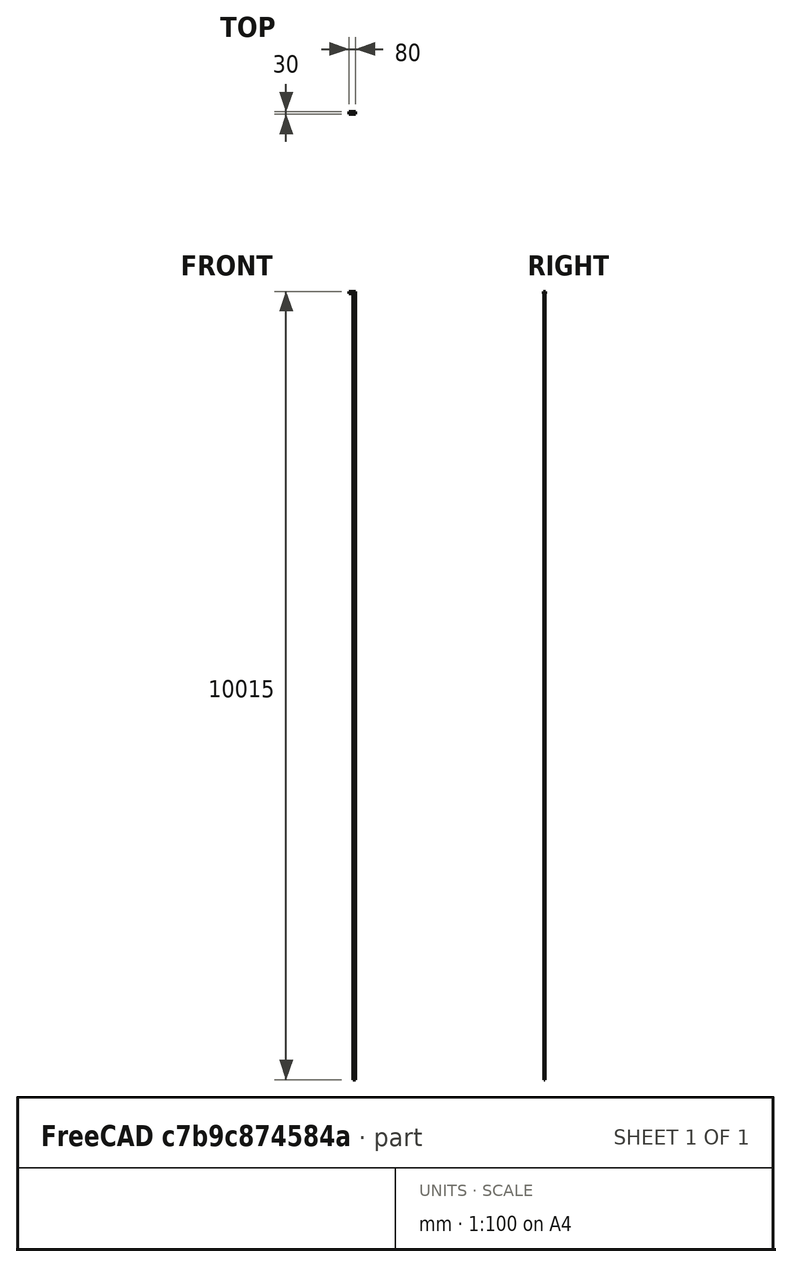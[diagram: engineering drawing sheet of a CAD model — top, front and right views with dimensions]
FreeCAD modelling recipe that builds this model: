
FCSTD DOCUMENT  (FreeCAD 0.14R3702 (Git))
Label: curso
License: CC-BY 3.0
LicenseURL: http://creativecommons.org/licenses/by/3.0/
objects: Sketcher::SketchObject×4, PartDesign::Pocket×2, PartDesign::Fillet×2, PartDesign::Pad×1
note: 12 computed .brp shape members not serialized (recipe doc carries the construction recipe); baked Part::Feature solids carry a one-line shape summary decoded from their .brp

FEATURE [Sketcher::SketchObject] Sketch002
  Placement = pos=(0,15.4858,0) rot=(0,0.707107,0.707107;3.14159rad)
  Support = -> Fillet001 [Face1]
  sketch-geometry (4):
    g0: LineSegment StartX=-40 StartY=15 StartZ=0 EndX=40 EndY=15 EndZ=0
    g1: LineSegment StartX=40 StartY=15 StartZ=0 EndX=40 EndY=-15 EndZ=0
    g2: LineSegment StartX=40 StartY=-15 StartZ=0 EndX=-40 EndY=-15 EndZ=0
    g3: LineSegment StartX=-40 StartY=-15 StartZ=0 EndX=-40 EndY=15 EndZ=0
  constraints (10):
    c: Coincident(g0,g1)
    c: Coincident(g1,g2)
    c: Coincident(g2,g3)
    c: Coincident(g3,g0)
    c: Symmetric(g0,g1,g-1)
    c: Symmetric(g2,g0,g-1)
    c: DistanceX(g0) = 80
    c: DistanceY(g3) = 30
    c: Vertical(g3)
    c: Horizontal(g0)
FEATURE [PartDesign::Pad] Pad
  Length = 30
  Length2 = 100
  Placement = pos=(0,15.4858,0) rot=(0,0.707107,0.707107;3.14159rad)
  Reversed = true
  Sketch = -> Sketch002
  Type = 0
FEATURE [Sketcher::SketchObject] Sketch
  ExternalGeometry = -> [Pad]
  Placement = pos=(0,15.4858,0) rot=(0,0.707107,0.707107;3.14159rad)
  Support = -> Pad [Face5]
  sketch-geometry (4):
    g0: LineSegment StartX=10 StartY=5 StartZ=0 EndX=40 EndY=5 EndZ=0
    g1: LineSegment StartX=40 StartY=5 StartZ=0 EndX=40 EndY=-5 EndZ=0
    g2: LineSegment StartX=40 StartY=-5 StartZ=0 EndX=10 EndY=-5 EndZ=0
    g3: LineSegment StartX=10 StartY=-5 StartZ=0 EndX=10 EndY=5 EndZ=0
  constraints (12):
    c: Coincident(g0,g1)
    c: Coincident(g1,g2)
    c: Coincident(g2,g3)
    c: Coincident(g3,g0)
    c: Horizontal(g0)
    c: Horizontal(g2)
    c: Vertical(g1)
    c: Vertical(g3)
    c: Symmetric(g2,g0,g-1)
    c: PointOnObject(g0,g-3)
    c: DistanceX(g0) = 30
    c: DistanceY(g3) = 10
FEATURE [PartDesign::Pocket] Pocket
  Length = 5
  Placement = pos=(0,15.4858,0) rot=(0,0.707107,0.707107;3.14159rad)
  Sketch = -> Sketch
  Type = 1
FEATURE [Sketcher::SketchObject] Sketch003
  Placement = pos=(0,15.4858,15) rot=(0,0,1;0rad)
  Support = -> Pocket [Face1]
FEATURE [Sketcher::SketchObject] Sketch004
  ExternalGeometry = -> [Pocket]
  Placement = pos=(0,15.4858,15) rot=(0,0,1;0rad)
  Support = -> Pocket [Face1]
  sketch-geometry (4):
    g0: LineSegment StartX=10 StartY=-10 StartZ=0 EndX=40 EndY=-10 EndZ=0
    g1: LineSegment StartX=40 StartY=-10 StartZ=0 EndX=40 EndY=-20 EndZ=0
    g2: LineSegment StartX=40 StartY=-20 StartZ=0 EndX=10 EndY=-20 EndZ=0
    g3: LineSegment StartX=10 StartY=-20 StartZ=0 EndX=10 EndY=-10 EndZ=0
  constraints (12):
    c: Coincident(g0,g1)
    c: Coincident(g1,g2)
    c: Coincident(g2,g3)
    c: Coincident(g3,g0)
    c: Horizontal(g0)
    c: Horizontal(g2)
    c: Vertical(g1)
    c: Vertical(g3)
    c: PointOnObject(g0,g-3)
    c: Distance(g0) = 30
    c: Distance(g3) = 10
    c: DistanceY(g-3,g0) = -10
FEATURE [PartDesign::Pocket] Pocket001
  Length = 5
  Placement = pos=(0,15.4858,0) rot=(0,0.707107,0.707107;3.14159rad)
  Sketch = -> Sketch004
  Type = 1
FEATURE [PartDesign::Fillet] Fillet
  Base = -> Pocket001 [Edge25,Edge4,Edge8,Edge32]
  Placement = pos=(0,15.4858,0) rot=(0,0.707107,0.707107;3.14159rad)
  Radius = 14.9999
FEATURE [PartDesign::Fillet] Fillet001
  Base = -> Fillet [Edge33,Edge17,Edge10,Edge21]
  Placement = pos=(0,15.4858,0) rot=(0,0.707107,0.707107;3.14159rad)
  Radius = 14.9999
